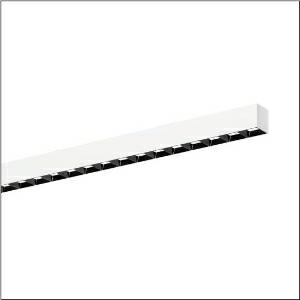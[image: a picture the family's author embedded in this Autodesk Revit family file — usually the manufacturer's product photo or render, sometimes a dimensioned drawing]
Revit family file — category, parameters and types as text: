
# Revit family: silica_21_51mx21tat4w
name_source: partatom
category: Lighting Fixtures
units: mm (PartAtom-declared; Revit-internal decimal feet)

## family parameters
Cut with Voids When Loaded = No
Host = Face
Light Source = No
Part Type = Normal
Room Calculation Point = No
Round Connector Dimension = Use Diameter
Shared = No

## types (1)
- --- (1 x LED, 3720 lm, 32.2 W, 6500K)
    Apparent Load = 32 VA
    CIE Flux Codes = 85 99 100 100 100
    Color Rendering = 80
    Color Temperature = 6500K
    Default Elevation = 1800 mm
    Description = Silica 21, office luminaire, primary light control with darklight reflector, of PMMA, black, CAT 2 (L<= 3000cd/m²), light emission: direct distribution, primary light characteristic: symmetric, installation type: surface-mounted, LED, rated luminous flux: 3.720lm, luminous efficacy: 110lm/W, light colour: 8tw, colour temperature: 2700..6500K, control gear: DALI DT8, with terminal, 3+2-pole, max. 2.5mm², mains connection: 220..240V, AC, 50/60Hz, rated input power: 33.8W, luminaire housing, of aluminium, traffic white (RAL 9016), length: 1.204mm, width: 53mm, height: 53mm, protection rating (complete): IP20, insulation class (complete): insulation class I (protective earthing), certification: CE, permissible operating ambient temperature: 0..+35°C, standard: EN 50419, packaging unit: 1 piece
    Height = 53 mm
    Lamp = 1 x LED
    Lamp Light Flux = 3720 lm
    Lamp Power = 32.2 W
    Lamp count = 1
    Length = 1204 mm
    Luminous efficacy = 116 lm/W
    Manufacturer = Siteco
    ModVariant = No
    Model = 51MX21TAT4W
    Mounting Place = Ceiling
    Mounting Type = Surface mounted
    Number of Poles = 1
    OnlyDefault = Yes
    Power Factor = 1
    Product Name = Silica 21
    Product group = office luminaire | ceiling mounted
    ProductGroupID = 301
    Protection Class = Protection class I
    Protection Degree = IP 20
    RLX_Detail_Level = 1
    RLX_Emergency_Light_Flux = 0 lm
    RLX_Emergency_Type = 0
    RLX_Emergency_Type_DB = No
    RlxData = <blob elided: 37801 chars, md5=c0765a47>
    Socket = socket
    Standby Power = 0 W
    System Light Flux = 3720 lm
    System Power = 32 W
    Type Comments = individual setting
    Type Image = l_1335873.jpg
    URL = http://relux.com
    VarID = @adj_139583
    Voltage = 0 V
    Weight = 0.00 kg
    Width = 53 mm

## geometry (parser evidence)
native form markers: Blend x4, Sweep x8
no freeform markers — native parametric forms only
